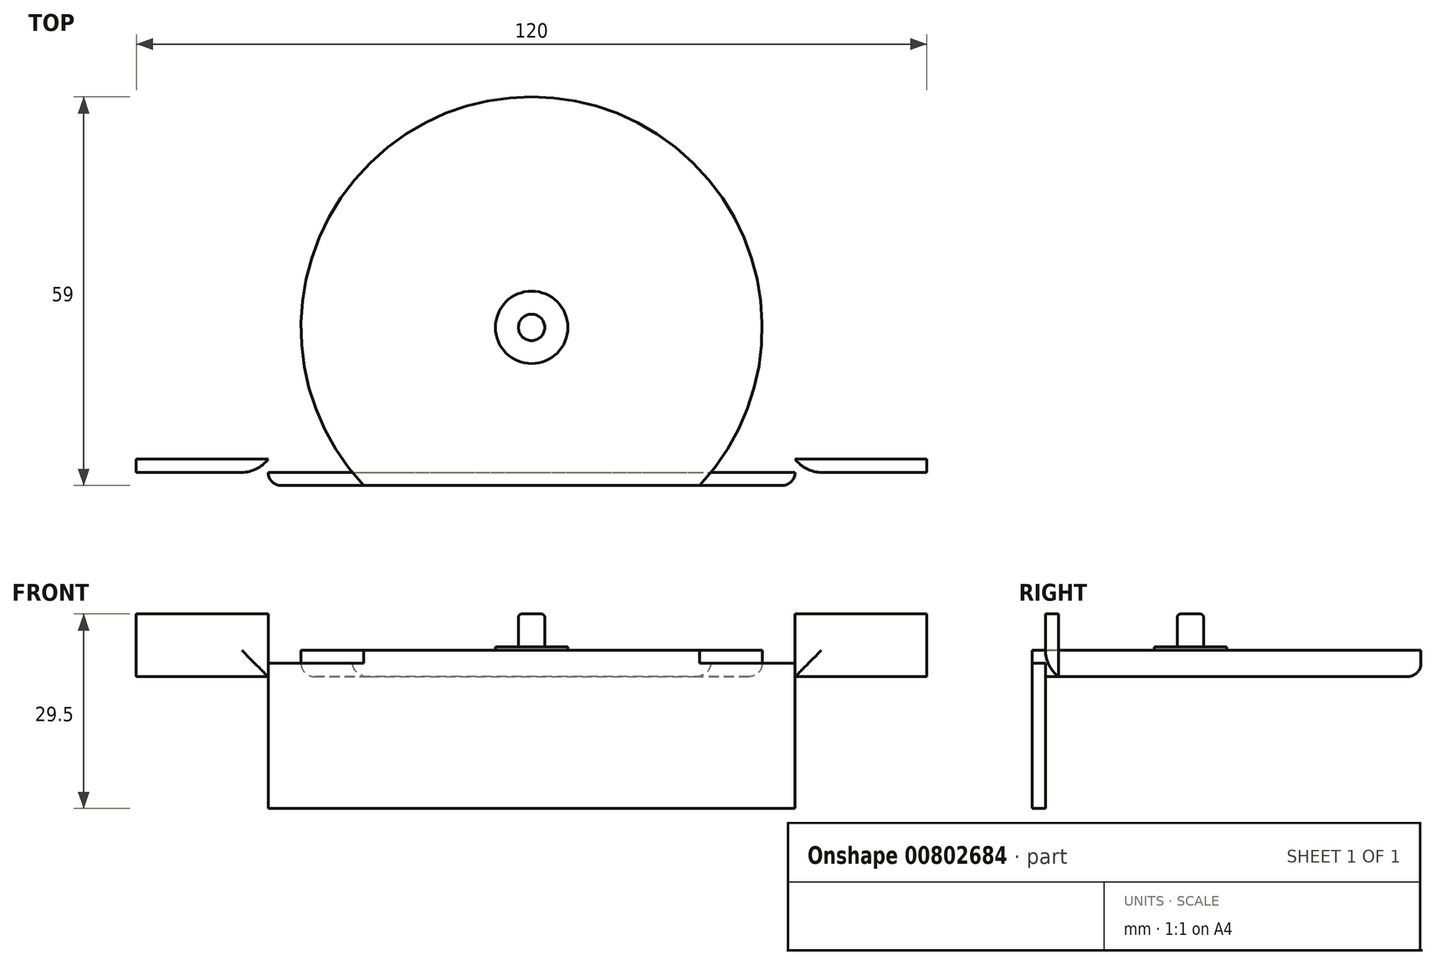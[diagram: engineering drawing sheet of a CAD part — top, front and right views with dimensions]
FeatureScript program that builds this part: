
annotation { "Feature Type Name" : "Feature", "Feature Type Description" : "" }
export const myFeature = defineFeature(function(context is Context, id is Id, definition is map)
    precondition{}
    {
        {
            var Q0;
            Q0=qCreatedBy(makeId("Top.planeOp"),FACE);
            var sketch = newSketch(context, id + "F0", { "sketchPlane" : qUnion([Q0])});
            skCircle(sketch, "E0", {"center": v(-115.15, 146.92) * mm, "radius": 35 * mm});
            skCircle(sketch, "E1", {"center": v(-115.15, 146.92) * mm, "radius": 5.5 * mm});
            skCircle(sketch, "E2", {"center": v(-115.15, 146.92) * mm, "radius": 2 * mm});
            skLineSegment(sketch, "E3.bottom", {"start": v(-175.15, 124.92) * mm, "end": v(-55.15, 124.92) * mm});
            skLineSegment(sketch, "E3.top", {"start": v(-175.15, 122.92) * mm, "end": v(-55.15, 122.92) * mm});
            skLineSegment(sketch, "E3.left", {"start": v(-175.15, 124.92) * mm, "end": v(-175.15, 122.92) * mm});
            skLineSegment(sketch, "E3.right", {"start": v(-55.15, 124.92) * mm, "end": v(-55.15, 122.92) * mm});
            skPoint(sketch, "E4", {"position": v(-115.15, 124.92) * mm});
            skLineSegment(sketch, "E5.bottom", {"start": v(-175.15, 126.92) * mm, "end": v(-155.15, 126.92) * mm});
            skLineSegment(sketch, "E5.top", {"start": v(-175.15, 122.92) * mm, "end": v(-155.15, 122.92) * mm});
            skLineSegment(sketch, "E5.left", {"start": v(-175.15, 126.92) * mm, "end": v(-175.15, 122.92) * mm});
            skLineSegment(sketch, "E5.right", {"start": v(-155.15, 126.92) * mm, "end": v(-155.15, 122.92) * mm});
            skLineSegment(sketch, "E6.bottom", {"start": v(-55.15, 126.92) * mm, "end": v(-75.15, 126.92) * mm});
            skLineSegment(sketch, "E6.top", {"start": v(-55.15, 122.92) * mm, "end": v(-75.15, 122.92) * mm});
            skLineSegment(sketch, "E6.left", {"start": v(-55.15, 126.92) * mm, "end": v(-55.15, 122.92) * mm});
            skLineSegment(sketch, "E6.right", {"start": v(-75.15, 126.92) * mm, "end": v(-75.15, 122.92) * mm});
            skSolve(sketch);
        }
        {
            var Q0;
            Q0=makeQuery(id+"F0.imprint","IMPRINT",FACE,{"disambiguationData":[TD([[makeQuery(id+"F0.imprint","IMPRINT",EDGE,{"derivedFrom":sQuery(id+"F0.wireOp",EDGE,"E1")}),-1.0]])]});
            var Q1;
            {var subQ0=sQuery(id+"F0.wireOp",EDGE,"E3.top");var subQ1=sQuery(id+"F0.wireOp",EDGE,"E0");var subQ2=makeQuery(id+"F0.imprint","INTERSECT",VERTEX,{"disambiguationData":[OD(0.0)],"derivedFrom":[subQ1,subQ0]});Q1=makeQuery(id+"F0.imprint","IMPRINT",FACE,{"disambiguationData":[TD([[makeQuery(id+"F0.imprint","IMPRINT",EDGE,{"disambiguationData":[TD([[subQ2,1.0]])],"derivedFrom":subQ1}),1.0]])]});}
            extrude(context, id + "F1", {"entities" : qUnion([Q0, Q1]), "depth" : 4 * mm, "offsetDistance" : 25 * mm});
        }
        {
            var Q0;
            Q0=makeQuery(id+"F0.imprint","IMPRINT",FACE,{"disambiguationData":[TD([[makeQuery(id+"F0.imprint","IMPRINT",EDGE,{"derivedFrom":sQuery(id+"F0.wireOp",EDGE,"E1")}),1.0]])]});
            extrude(context, id + "F2", {"entities" : qUnion([Q0]), "operationType" : NewBodyOperationType.ADD, "depth" : 4.5 * mm, "offsetDistance" : 25 * mm});
        }
        {
            var Q0;
            Q0=makeQuery(id+"F0.imprint","IMPRINT",FACE,{"disambiguationData":[TD([[makeQuery(id+"F0.imprint","IMPRINT",EDGE,{"derivedFrom":sQuery(id+"F0.wireOp",EDGE,"E2")}),1.0]])]});
            extrude(context, id + "F3", {"entities" : qUnion([Q0]), "operationType" : NewBodyOperationType.ADD, "depth" : 9.5 * mm, "offsetDistance" : 25 * mm});
        }
        {
            var Q0;
            {var subQ0=sQuery(id+"F0.wireOp",EDGE,"E3.top");var subQ1=sQuery(id+"F0.wireOp",EDGE,"E0");var subQ2=makeQuery(id+"F0.imprint","INTERSECT",VERTEX,{"disambiguationData":[OD(0.0)],"derivedFrom":[subQ1,subQ0]});Q0=makeQuery(id+"F0.imprint","IMPRINT",FACE,{"disambiguationData":[TD([[makeQuery(id+"F0.imprint","IMPRINT",EDGE,{"disambiguationData":[TD([[subQ2,1.0]])],"derivedFrom":subQ1}),-1.0]])]});}
            var Q1;
            {var subQ0=sQuery(id+"F0.wireOp",EDGE,"E3.top");var subQ1=sQuery(id+"F0.wireOp",EDGE,"E0");var subQ2=makeQuery(id+"F0.imprint","INTERSECT",VERTEX,{"disambiguationData":[OD(1.0)],"derivedFrom":[subQ1,subQ0]});Q1=makeQuery(id+"F0.imprint","IMPRINT",FACE,{"disambiguationData":[TD([[makeQuery(id+"F0.imprint","IMPRINT",EDGE,{"disambiguationData":[TD([[subQ2,-1.0]])],"derivedFrom":subQ1}),-1.0]])]});}
            var Q2;
            {var subQ5=sQuery(id+"F0.wireOp",EDGE,"E6.top");Q2=makeQuery(id+"F0.imprint","IMPRINT",FACE,{"disambiguationData":[TD([[makeQuery(id+"F0.imprint","IMPRINT",EDGE,{"derivedFrom":subQ5}),-1.0]])]});}
            var Q3;
            {var subQ5=sQuery(id+"F0.wireOp",EDGE,"E5.top");Q3=makeQuery(id+"F0.imprint","IMPRINT",FACE,{"disambiguationData":[TD([[makeQuery(id+"F0.imprint","IMPRINT",EDGE,{"derivedFrom":subQ5}),1.0]])]});}
            extrude(context, id + "F4", {"entities" : qUnion([Q0, Q1, Q2, Q3]), "operationType" : NewBodyOperationType.ADD, "depth" : 2 * mm, "offsetDistance" : 25 * mm});
        }
        {
            var Q0;
            {var subQ5=sQuery(id+"F0.wireOp",EDGE,"E6.top");Q0=makeQuery(id+"F0.imprint","IMPRINT",FACE,{"disambiguationData":[TD([[makeQuery(id+"F0.imprint","IMPRINT",EDGE,{"derivedFrom":subQ5}),-1.0]])]});}
            var Q1;
            {var subQ0=sQuery(id+"F0.wireOp",EDGE,"E3.top");var subQ1=sQuery(id+"F0.wireOp",EDGE,"E0");var subQ2=makeQuery(id+"F0.imprint","INTERSECT",VERTEX,{"disambiguationData":[OD(1.0)],"derivedFrom":[subQ1,subQ0]});Q1=makeQuery(id+"F0.imprint","IMPRINT",FACE,{"disambiguationData":[TD([[makeQuery(id+"F0.imprint","IMPRINT",EDGE,{"disambiguationData":[TD([[subQ2,-1.0]])],"derivedFrom":subQ1}),-1.0]])]});}
            var Q2;
            {var subQ0=sQuery(id+"F0.wireOp",EDGE,"E3.top");var subQ1=sQuery(id+"F0.wireOp",EDGE,"E0");var subQ2=makeQuery(id+"F0.imprint","INTERSECT",VERTEX,{"disambiguationData":[OD(0.0)],"derivedFrom":[subQ1,subQ0]});Q2=makeQuery(id+"F0.imprint","IMPRINT",FACE,{"disambiguationData":[TD([[makeQuery(id+"F0.imprint","IMPRINT",EDGE,{"disambiguationData":[TD([[subQ2,1.0]])],"derivedFrom":subQ1}),1.0]])]});}
            var Q3;
            {var subQ0=sQuery(id+"F0.wireOp",EDGE,"E3.top");var subQ1=sQuery(id+"F0.wireOp",EDGE,"E0");var subQ2=makeQuery(id+"F0.imprint","INTERSECT",VERTEX,{"disambiguationData":[OD(0.0)],"derivedFrom":[subQ1,subQ0]});Q3=makeQuery(id+"F0.imprint","IMPRINT",FACE,{"disambiguationData":[TD([[makeQuery(id+"F0.imprint","IMPRINT",EDGE,{"disambiguationData":[TD([[subQ2,1.0]])],"derivedFrom":subQ1}),-1.0]])]});}
            var Q4;
            {var subQ5=sQuery(id+"F0.wireOp",EDGE,"E5.top");Q4=makeQuery(id+"F0.imprint","IMPRINT",FACE,{"disambiguationData":[TD([[makeQuery(id+"F0.imprint","IMPRINT",EDGE,{"derivedFrom":subQ5}),1.0]])]});}
            extrude(context, id + "F5", {"entities" : qUnion([Q0, Q1, Q2, Q3, Q4]), "operationType" : NewBodyOperationType.ADD, "oppositeDirection" : true, "depth" : 20 * mm, "offsetDistance" : 25 * mm});
        }
        {
            var Q0;
            {var subQ5=sQuery(id+"F0.wireOp",EDGE,"E5.bottom");Q0=makeQuery(id+"F0.imprint","IMPRINT",FACE,{"disambiguationData":[TD([[makeQuery(id+"F0.imprint","IMPRINT",EDGE,{"derivedFrom":subQ5}),-1.0]])]});}
            var Q1;
            {var subQ5=sQuery(id+"F0.wireOp",EDGE,"E6.bottom");Q1=makeQuery(id+"F0.imprint","IMPRINT",FACE,{"disambiguationData":[TD([[makeQuery(id+"F0.imprint","IMPRINT",EDGE,{"derivedFrom":subQ5}),1.0]])]});}
            var Q2;
            Q2=makeQuery(id+"F3.opExtrude","CAP_FACE",FACE,{"disambiguationData":[OSD([sQuery(id+"F0.wireOp",EDGE,"E2")])],"isStart":false});
            extrude(context, id + "F6", {"entities" : qUnion([Q0, Q1]), "operationType" : NewBodyOperationType.ADD, "endBound" : BoundingType.UP_TO_SURFACE, "depth" : 25 * mm, "endBoundEntityFace" : qUnion([Q2]), "offsetDistance" : 25 * mm});
        }
        {
            var Q0;
            Q0=makeQuery(id+"F3.opExtrude","CAP_EDGE",EDGE,{"disambiguationData":[OSD([sQuery(id+"F0.wireOp",EDGE,"E2")])],"isStart":false});
            fillet(context, id + "F7", {"entities" : qUnion([Q0]), "radius" : .5 * mm, "tangentPropagation" : true, "allowEdgeOverflow" : false});
        }
        {
            var Q0;
            {var subQ0=sQuery(id+"F0.wireOp",EDGE,"E3.left");var subQ1=sQuery(id+"F0.wireOp",EDGE,"E3.top");Q0=makeQuery(id+"F5.boolean.opBoolean","MERGE",EDGE,{"derivedFrom":[makeQuery(id+"F4.opExtrude","SWEPT_EDGE",EDGE,{"disambiguationData":[OSD([subQ1,subQ0])]}),makeQuery(id+"F5.opExtrude","SWEPT_EDGE",EDGE,{"disambiguationData":[OSD([subQ1,subQ0])]})]});}
            var Q1;
            {var subQ0=sQuery(id+"F0.wireOp",EDGE,"E3.right");var subQ1=sQuery(id+"F0.wireOp",EDGE,"E3.top");Q1=makeQuery(id+"F5.boolean.opBoolean","MERGE",EDGE,{"derivedFrom":[makeQuery(id+"F4.opExtrude","SWEPT_EDGE",EDGE,{"disambiguationData":[OSD([subQ1,subQ0])]}),makeQuery(id+"F5.opExtrude","SWEPT_EDGE",EDGE,{"disambiguationData":[OSD([subQ1,subQ0])]})]});}
            var Q2;
            Q2=makeQuery(id+"F5.opExtrude","CAP_EDGE",EDGE,{"disambiguationData":[OSD([sQuery(id+"F0.wireOp",EDGE,"E3.bottom")])],"isStart":true});
            var Q3;
            {var subQ0=sQuery(id+"F0.wireOp",EDGE,"E0");Q3=makeQuery(id+"F4.opExtrude","CAP_EDGE",EDGE,{"disambiguationData":[OSD([subQ0]),TDD([makeQuery(id+"F0.imprint","IMPRINT",EDGE,{"disambiguationData":[TD([[makeQuery(id+"F0.imprint","INTERSECT",VERTEX,{"disambiguationData":[OD(1.0)],"derivedFrom":[subQ0,sQuery(id+"F0.wireOp",EDGE,"E3.top")]}),-1.0]])],"derivedFrom":subQ0})])],"isStart":false});}
            var Q4;
            {var subQ0=sQuery(id+"F0.wireOp",EDGE,"E0");Q4=makeQuery(id+"F4.opExtrude","CAP_EDGE",EDGE,{"disambiguationData":[OSD([subQ0]),TDD([makeQuery(id+"F0.imprint","IMPRINT",EDGE,{"disambiguationData":[TD([[makeQuery(id+"F0.imprint","INTERSECT",VERTEX,{"disambiguationData":[OD(0.0)],"derivedFrom":[subQ0,sQuery(id+"F0.wireOp",EDGE,"E3.top")]}),1.0]])],"derivedFrom":subQ0})])],"isStart":false});}
            var Q5;
            Q5=makeQuery(id+"F1.opExtrude","CAP_EDGE",EDGE,{"disambiguationData":[OSD([sQuery(id+"F0.wireOp",EDGE,"E0")])],"isStart":true});
            var Q6;
            {var subQ0=sQuery(id+"F0.wireOp",EDGE,"E5.left");var subQ1=sQuery(id+"F0.wireOp",EDGE,"E5.top");Q6=makeQuery(id+"F5.boolean.opBoolean","MERGE",EDGE,{"derivedFrom":[makeQuery(id+"F4.opExtrude","SWEPT_EDGE",EDGE,{"disambiguationData":[OSD([subQ1,subQ0])]}),makeQuery(id+"F5.opExtrude","SWEPT_EDGE",EDGE,{"disambiguationData":[OSD([subQ1,subQ0])]})]});}
            var Q7;
            {var subQ0=sQuery(id+"F0.wireOp",EDGE,"E6.left");var subQ1=sQuery(id+"F0.wireOp",EDGE,"E6.top");Q7=makeQuery(id+"F5.boolean.opBoolean","MERGE",EDGE,{"derivedFrom":[makeQuery(id+"F4.opExtrude","SWEPT_EDGE",EDGE,{"disambiguationData":[OSD([subQ1,subQ0])]}),makeQuery(id+"F5.opExtrude","SWEPT_EDGE",EDGE,{"disambiguationData":[OSD([subQ1,subQ0])]})]});}
            fillet(context, id + "F8", {"entities" : qUnion([Q0, Q1, Q2, Q3, Q4, Q5, Q6, Q7]), "radius" : 2 * mm, "tangentPropagation" : true, "allowEdgeOverflow" : false});
        }
        {
            var Q0;
            {var subQ0=sQuery(id+"F0.wireOp",EDGE,"E3.bottom");Q0=makeQuery(id+"F6.opExtrude","CAP_EDGE",EDGE,{"disambiguationData":[OSD([subQ0]),TDD([makeQuery(id+"F0.imprint","IMPRINT",EDGE,{"disambiguationData":[TD([[makeQuery(id+"F0.imprint","INTERSECT",VERTEX,{"derivedFrom":[subQ0,sQuery(id+"F0.wireOp",EDGE,"E6.left")]}),1.0]])],"derivedFrom":subQ0})])],"isStart":true});}
            var Q1;
            {var subQ0=sQuery(id+"F0.wireOp",EDGE,"E3.bottom");Q1=makeQuery(id+"F6.opExtrude","CAP_EDGE",EDGE,{"disambiguationData":[OSD([subQ0]),TDD([makeQuery(id+"F0.imprint","IMPRINT",EDGE,{"disambiguationData":[TD([[makeQuery(id+"F0.imprint","INTERSECT",VERTEX,{"derivedFrom":[subQ0,sQuery(id+"F0.wireOp",EDGE,"E5.left")]}),-1.0]])],"derivedFrom":subQ0})])],"isStart":true});}
            var Q2;
            {var subQ0=sQuery(id+"F0.wireOp",EDGE,"E3.bottom");var subQ2=sQuery(id+"F0.wireOp",EDGE,"E5.right");Q2=makeQuery(id+"F6.boolean.opBoolean","SPLIT",EDGE,{"disambiguationData":[topologyDisambiguationEdgeConnected([makeQuery(id+"F5.opExtrude","SWEPT_FACE",FACE,{"disambiguationData":[OSD([subQ0])]})])],"derivedFrom":makeQuery(id+"F6.opExtrude","SWEPT_EDGE",EDGE,{"disambiguationData":[OSD([subQ0,subQ2])]})});}
            var Q3;
            {var subQ0=sQuery(id+"F0.wireOp",EDGE,"E3.bottom");var subQ3=sQuery(id+"F0.wireOp",EDGE,"E6.right");Q3=makeQuery(id+"F6.boolean.opBoolean","SPLIT",EDGE,{"disambiguationData":[topologyDisambiguationEdgeConnected([makeQuery(id+"F5.opExtrude","SWEPT_FACE",FACE,{"disambiguationData":[OSD([subQ0])]})])],"derivedFrom":makeQuery(id+"F6.opExtrude","SWEPT_EDGE",EDGE,{"disambiguationData":[OSD([subQ0,subQ3])]})});}
            fillet(context, id + "F9", {"entities" : qUnion([Q0, Q1, Q2, Q3]), "radius" : 5 * mm, "tangentPropagation" : true, "allowEdgeOverflow" : false});
        }
    });
